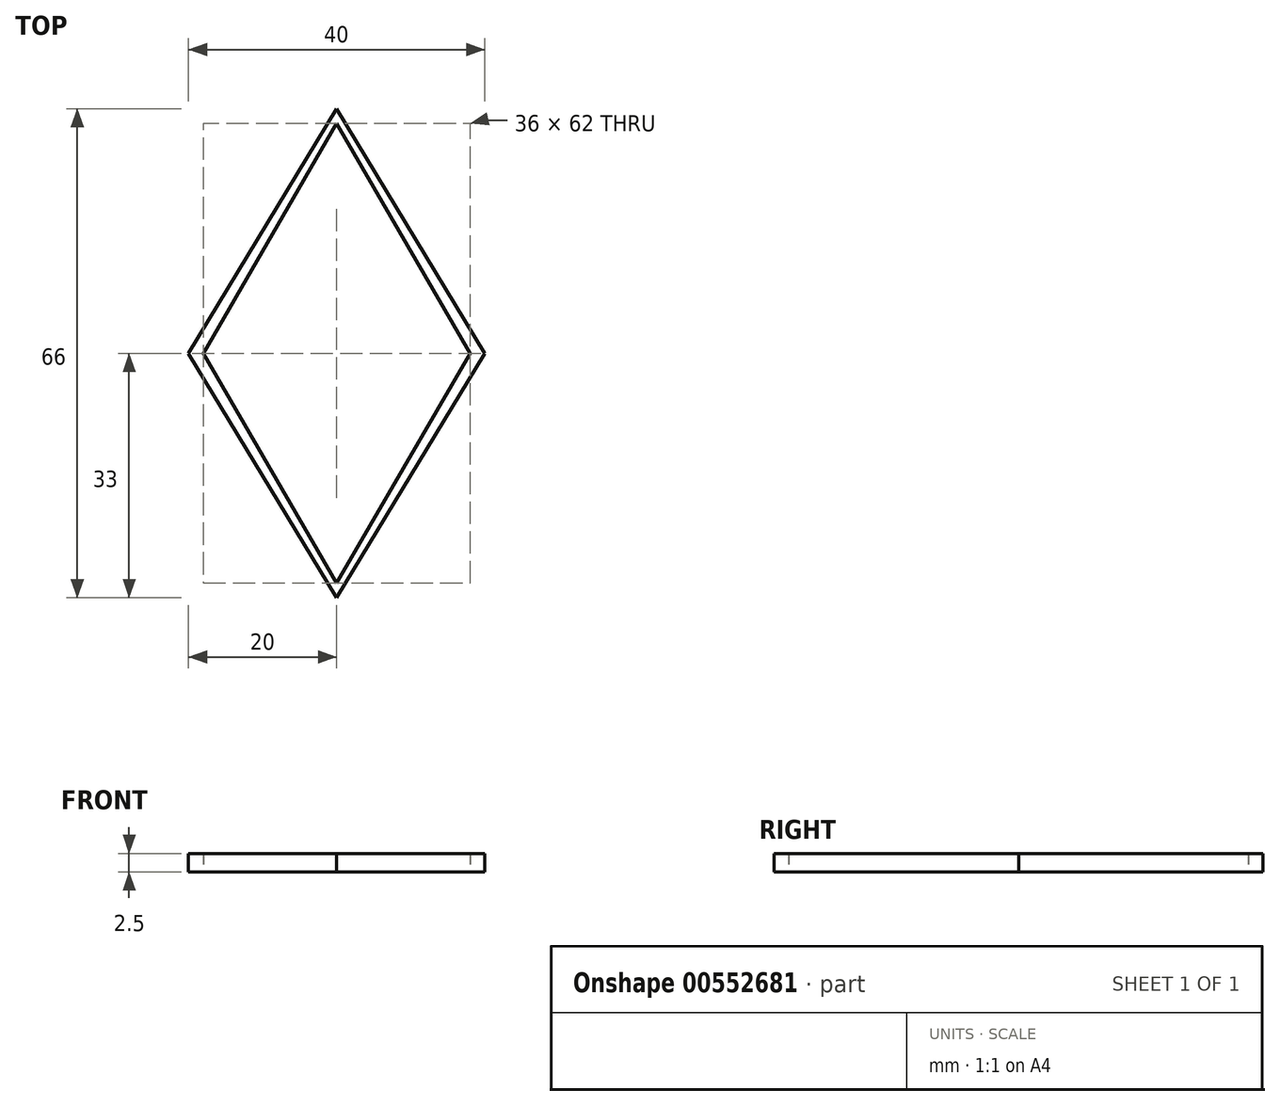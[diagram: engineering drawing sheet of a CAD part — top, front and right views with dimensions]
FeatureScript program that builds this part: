
annotation { "Feature Type Name" : "Feature", "Feature Type Description" : "" }
export const myFeature = defineFeature(function(context is Context, id is Id, definition is map)
    precondition{}
    {
        {
            var Q0;
            Q0=qCreatedBy(makeId("Top.planeOp"),FACE);
            var sketch = newSketch(context, id + "F0", { "sketchPlane" : qUnion([Q0])});
            skLineSegment(sketch, "E0", {"start": v(0, 0) * mm, "end": v(-20, 0) * mm});
            skLineSegment(sketch, "E1", {"start": v(0, 0) * mm, "end": v(20, 0) * mm});
            skLineSegment(sketch, "E2", {"start": v(0, 0) * mm, "end": v(0, 33) * mm});
            skLineSegment(sketch, "E3", {"start": v(0, 0) * mm, "end": v(0, -33) * mm});
            skLineSegment(sketch, "E4", {"start": v(0, -33) * mm, "end": v(-20, 0) * mm});
            skLineSegment(sketch, "E5", {"start": v(-20, 0) * mm, "end": v(0, 33) * mm});
            skLineSegment(sketch, "E6", {"start": v(0, 33) * mm, "end": v(20, 0) * mm});
            skLineSegment(sketch, "E7", {"start": v(20, 0) * mm, "end": v(0, -33) * mm});
            skLineSegment(sketch, "E8", {"start": v(-20, 0) * mm, "end": v(-18, 0) * mm});
            skLineSegment(sketch, "E9", {"start": v(0, 33) * mm, "end": v(0, 31) * mm});
            skLineSegment(sketch, "E10", {"start": v(20, 0) * mm, "end": v(18, 0) * mm});
            skLineSegment(sketch, "E11", {"start": v(0, -33) * mm, "end": v(0, -31) * mm});
            skLineSegment(sketch, "E12", {"start": v(-18, 0) * mm, "end": v(0, 31) * mm});
            skLineSegment(sketch, "E13", {"start": v(0, 31) * mm, "end": v(18, 0) * mm});
            skLineSegment(sketch, "E14", {"start": v(18, 0) * mm, "end": v(0, -31) * mm});
            skLineSegment(sketch, "E15", {"start": v(0, -31) * mm, "end": v(-18, 0) * mm});
            skLineSegment(sketch, "E16", {"start": v(-10, 13.78) * mm, "end": v(10.5, -12.91) * mm});
            skPoint(sketch, "E16.startSnap0", {"position": v(-10, 16.5) * mm});
            skSolve(sketch);
        }
        {
            var Q0;
            Q0=makeQuery(id+"F0.imprint","IMPRINT",FACE,{"disambiguationData":[TD([[makeQuery(id+"F0.imprint","IMPRINT",EDGE,{"derivedFrom":sQuery(id+"F0.wireOp",EDGE,"E5")}),-1.0]])]});
            var Q1;
            Q1=makeQuery(id+"F0.imprint","IMPRINT",FACE,{"disambiguationData":[TD([[makeQuery(id+"F0.imprint","IMPRINT",EDGE,{"derivedFrom":sQuery(id+"F0.wireOp",EDGE,"E4")}),-1.0]])]});
            var Q2;
            Q2=makeQuery(id+"F0.imprint","IMPRINT",FACE,{"disambiguationData":[TD([[makeQuery(id+"F0.imprint","IMPRINT",EDGE,{"derivedFrom":sQuery(id+"F0.wireOp",EDGE,"E7")}),-1.0]])]});
            var Q3;
            Q3=makeQuery(id+"F0.imprint","IMPRINT",FACE,{"disambiguationData":[TD([[makeQuery(id+"F0.imprint","IMPRINT",EDGE,{"derivedFrom":sQuery(id+"F0.wireOp",EDGE,"E6")}),-1.0]])]});
            extrude(context, id + "F1", {"entities" : qUnion([Q0, Q1, Q2, Q3]), "depth" : 2.5 * mm, "offsetDistance" : 25 * mm});
        }
    });
